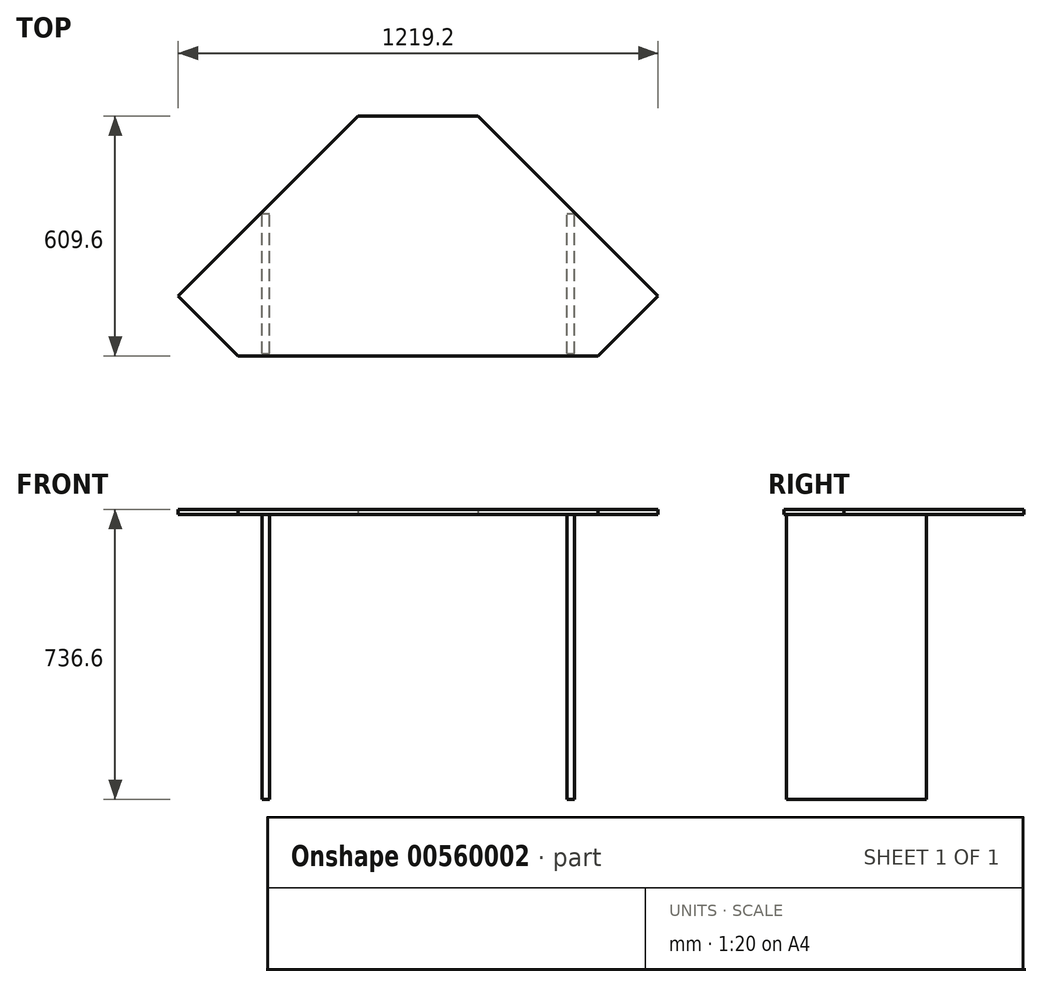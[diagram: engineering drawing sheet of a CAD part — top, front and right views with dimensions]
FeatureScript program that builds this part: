
annotation { "Feature Type Name" : "Feature", "Feature Type Description" : "" }
export const myFeature = defineFeature(function(context is Context, id is Id, definition is map)
    precondition{}
    {
        {
            var Q0;
            Q0=qCreatedBy(makeId("Top.planeOp"),FACE);
            var sketch = newSketch(context, id + "F0", { "sketchPlane" : qUnion([Q0])});
            skLineSegment(sketch, "E0", {"start": v(-152.4, 609.6) * mm, "end": v(152.4, 609.6) * mm});
            skLineSegment(sketch, "E1", {"start": v(-609.6, 152.4) * mm, "end": v(-152.4, 609.6) * mm});
            skLineSegment(sketch, "E2", {"start": v(457.2, 0) * mm, "end": v(-457.2, 0) * mm});
            skLineSegment(sketch, "E3", {"start": v(609.6, 152.4) * mm, "end": v(152.4, 609.6) * mm});
            skLineSegment(sketch, "E4", {"start": v(152.4, 609.6) * mm, "end": v(0, 762) * mm, "construction": true});
            skLineSegment(sketch, "E5", {"start": v(-152.4, 609.6) * mm, "end": v(0, 762) * mm, "construction": true});
            skLineSegment(sketch, "E6", {"start": v(0, 0) * mm, "end": v(0, 609.6) * mm, "construction": true});
            skLineSegment(sketch, "E7", {"start": v(-609.6, 152.4) * mm, "end": v(-457.2, 0) * mm});
            skLineSegment(sketch, "E8", {"start": v(609.6, 152.4) * mm, "end": v(457.2, 0) * mm});
            skSolve(sketch);
        }
        {
            var Q0;
            Q0 = qSketchRegion(id + "F0", true);
            extrude(context, id + "F1", {"entities" : qUnion([Q0]), "depth" : 12.7 * mm, "offsetDistance" : 25.4 * mm});
        }
        {
            var Q0;
            Q0=makeQuery(id+"F1.opExtrude","CAP_FACE",FACE,{"disambiguationData":[OSD([sQuery(id+"F0.wireOp",EDGE,"E0"),sQuery(id+"F0.wireOp",EDGE,"E1"),sQuery(id+"F0.wireOp",EDGE,"E2"),sQuery(id+"F0.wireOp",EDGE,"E3"),sQuery(id+"F0.wireOp",EDGE,"E7"),sQuery(id+"F0.wireOp",EDGE,"E8")])],"isStart":true});
            var sketch = newSketch(context, id + "F2", { "sketchPlane" : qUnion([Q0])});
            skLineSegment(sketch, "E9.bottom", {"start": v(-396.88, -6.35) * mm, "end": v(-377.82, -6.35) * mm});
            skLineSegment(sketch, "E9.top", {"start": v(-396.88, -361.95) * mm, "end": v(-377.83, -361.95) * mm});
            skLineSegment(sketch, "E9.left", {"start": v(-396.88, -6.35) * mm, "end": v(-396.88, -361.95) * mm});
            skLineSegment(sketch, "E9.right", {"start": v(-377.82, -6.35) * mm, "end": v(-377.82, -361.95) * mm});
            skLineSegment(sketch, "E10.bottom", {"start": v(377.83, -6.35) * mm, "end": v(396.88, -6.35) * mm});
            skLineSegment(sketch, "E10.top", {"start": v(377.83, -361.95) * mm, "end": v(396.88, -361.95) * mm});
            skLineSegment(sketch, "E10.left", {"start": v(377.83, -6.35) * mm, "end": v(377.83, -361.95) * mm});
            skLineSegment(sketch, "E10.right", {"start": v(396.88, -6.35) * mm, "end": v(396.88, -361.95) * mm});
            skLineSegment(sketch, "E11", {"start": v(0, 0) * mm, "end": v(0, -152.4) * mm, "construction": true});
            skSolve(sketch);
        }
        {
            var Q0;
            Q0 = qSketchRegion(id + "F2", true);
            extrude(context, id + "F3", {"entities" : qUnion([Q0]), "depth" : 723.9 * mm, "offsetDistance" : 25.4 * mm});
        }
    });
